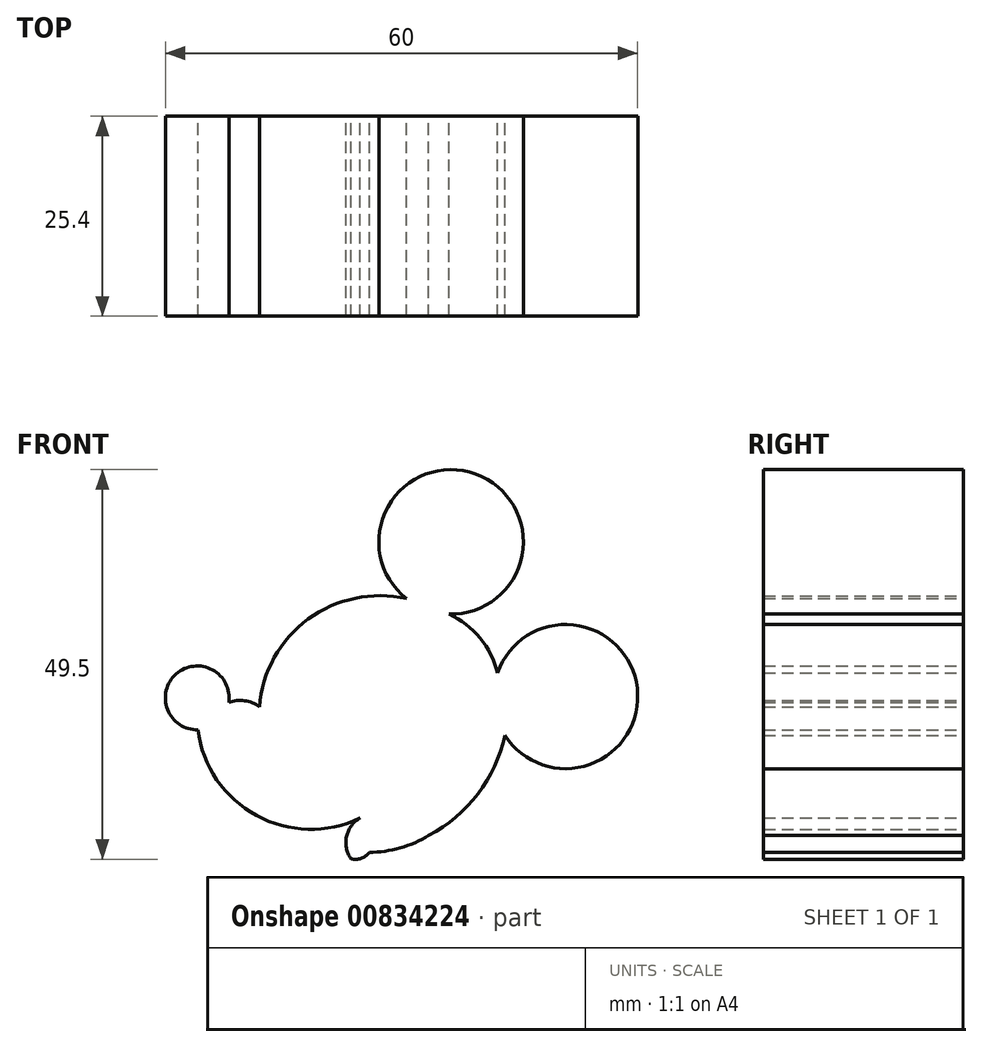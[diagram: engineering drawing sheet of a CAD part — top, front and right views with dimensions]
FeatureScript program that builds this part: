
annotation { "Feature Type Name" : "Feature", "Feature Type Description" : "" }
export const myFeature = defineFeature(function(context is Context, id is Id, definition is map)
    precondition{}
    {
        {
            var Q0;
            Q0=qCreatedBy(makeId("Front.planeOp"),FACE);
            var sketch = newSketch(context, id + "F0", { "sketchPlane" : qUnion([Q0])});
            skArc(sketch, "E0", {"start": v(44.18, 46.92) * mm, "mid": v(47.57, 64.73) * mm, "end": v(38.76, 48.88) * mm});
            skArc(sketch, "E1", {"start": v(50.35, 39.45) * mm, "mid": v(48.12, 43.89) * mm, "end": v(44.18, 46.92) * mm});
            skArc(sketch, "E2", {"start": v(51.28, 31.5) * mm, "mid": v(68.1, 37.5) * mm, "end": v(50.35, 39.45) * mm});
            skArc(sketch, "E3", {"start": v(41.6, 18.79) * mm, "mid": v(47.84, 24.08) * mm, "end": v(51.28, 31.5) * mm});
            skArc(sketch, "E4", {"start": v(34.06, 16.65) * mm, "mid": v(37.97, 17.22) * mm, "end": v(41.6, 18.79) * mm});
            skArc(sketch, "E5", {"start": v(31.72, 15.85) * mm, "mid": v(33, 15.9) * mm, "end": v(34.06, 16.65) * mm});
            skArc(sketch, "E6", {"start": v(33.26, 21.2) * mm, "mid": v(31.21, 18.88) * mm, "end": v(31.72, 15.85) * mm});
            skArc(sketch, "E7", {"start": v(12.28, 32.22) * mm, "mid": v(19.9, 21.24) * mm, "end": v(33.26, 21.2) * mm});
            skArc(sketch, "E8", {"start": v(16.22, 35.69) * mm, "mid": v(9.52, 39.31) * mm, "end": v(12.28, 32.22) * mm});
            skArc(sketch, "E9", {"start": v(20.1, 35.16) * mm, "mid": v(18.22, 35.9) * mm, "end": v(16.22, 35.69) * mm});
            skArc(sketch, "E10", {"start": v(38.76, 48.88) * mm, "mid": v(26.3, 46.28) * mm, "end": v(20.1, 35.16) * mm});
            skSolve(sketch);
        }
        {
            var Q0;
            Q0 = qSketchRegion(id + "F0", true);
            extrude(context, id + "F1", {"entities" : qUnion([Q0]), "depth" : 25.4 * mm, "offsetDistance" : 25.4 * mm});
        }
    });
